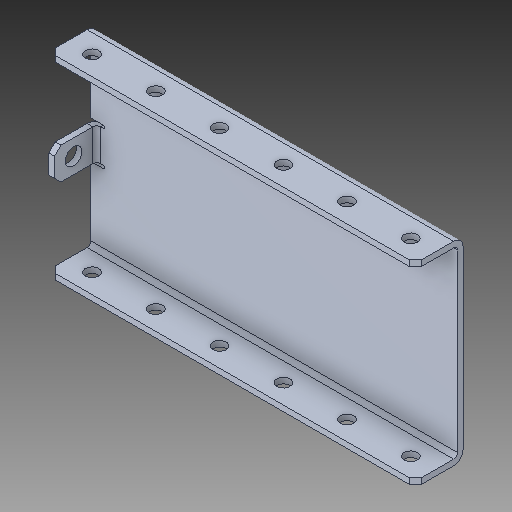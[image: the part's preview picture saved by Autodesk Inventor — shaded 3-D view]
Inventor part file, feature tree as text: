
AUTODESK INVENTOR PART (.ipt)
format: ipt  version: 2018.2 (Build 222227000, 227)  size: 157,696 bytes
history: native  units: in
note: dims shown in document units (in); Inventor stores cm internally (conversion verified against a paired STEP export)
features: chamfer x1
ambient origin geometry x8: Origin, YZ Plane, XZ Plane, XY Plane, X Axis, Y Axis, Z Axis, Center Point
bodies: Solid1 (feature_tree)
feature tree (1):
  chamfer  "Chamfer1"  [1 undecoded]
note: 1 required parameter value undecoded (feature->parameter linkage not recoverable at this tier; creation-order binding heuristic only, values carry confidence <= 0.55)
